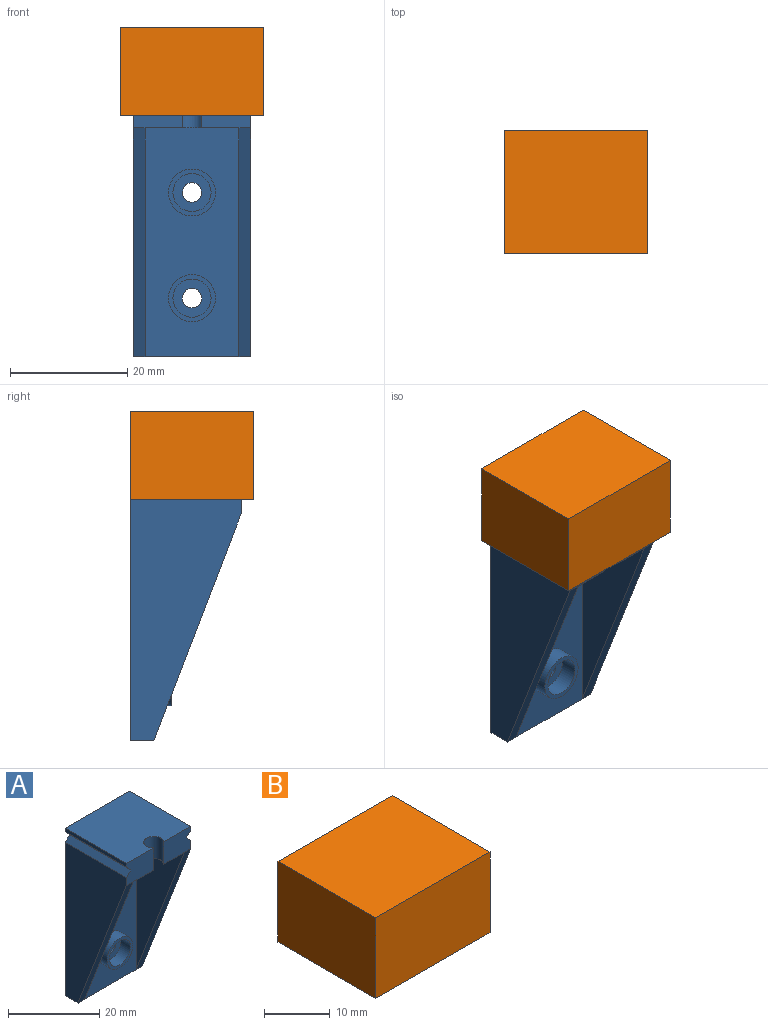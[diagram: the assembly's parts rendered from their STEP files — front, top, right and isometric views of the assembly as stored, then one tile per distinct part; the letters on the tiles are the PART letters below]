
ASSEMBLY  parts=2 mates=1
PART A: 30 faces, bbox 20x19x45 mm
  f0: plane 8.39x6mm, normal (0,-1,0), area 48.3mm2, adj f2,f4,f5,f11,f12,f13,f27,f29
  f1: plane 8.39x6mm, normal (0,-1,0), area 48.3mm2, adj f2,f5,f6,f7,f8,f9,f28,f29
  f2: plane 16x15mm, normal (0,0,-1), area 226.4mm2, adj f0,f1,f3,f25,f26,f29
  f3: plane 39x16mm, normal (0,-1,0), area 523.5mm2, adj f2,f10,f15,f17,f25,f26
  f4: plane 19x1mm, normal (1,0,0), area 19mm2, adj f0,f5,f13,f14
  f5: plane 20x19mm, normal (0,0,1), area 366.4mm2, adj f0,f1,f4,f6,f14,f29
  f6: plane 19x1mm, normal (-1,0,0), area 19mm2, adj f1,f5,f7,f14
  f7: plane 19x1.41mm, normal (-0.71,0,-0.71), area 38mm2, adj f1,f6,f8,f14
  f8: plane 19x1.41mm, normal (-0.71,0,0.71), area 38mm2, adj f1,f7,f9,f14
  f9: plane 41.17x19mm, normal (-1,0,0), area 489.8mm2, adj f1,f8,f10,f14,f28
  f10: plane 20x4mm, normal (0,0,-1), area 80mm2, adj f3,f9,f11,f14,f27,f28
  f11: plane 41.17x19mm, normal (1,0,0), area 489.8mm2, adj f0,f10,f12,f14,f27
  f12: plane 19x1.41mm, normal (0.71,0,0.71), area 38mm2, adj f0,f11,f13,f14
  f13: plane 19x1.41mm, normal (0.71,0,-0.71), area 38mm2, adj f0,f4,f12,f14
  f14: plane 45x20mm, normal (0,1,0), area 878.9mm2, adj f4,f5,f6,f7,f8,f9,f10,f11
  f15: cylinder r=4mm len=8mm, axis (0,1,0), area 75.4mm2, adj f3,f16
  f16: plane 8x8mm, normal (0,-1,0), area 17.1mm2, adj f15,f21
  f17: cylinder r=4mm len=8mm, axis (0,1,0), area 75.4mm2, adj f3,f18
  f18: plane 8x8mm, normal (0,-1,0), area 17.1mm2, adj f17,f24
  f19: cylinder r=1.65mm len=4mm, axis (0,-1,0), area 41.5mm2, adj f14,f20
  f20: plane 6.5x6.5mm, normal (0,-1,0), area 24.6mm2, adj f19,f21
  f21: cylinder r=3.25mm len=6.5mm, axis (0,-1,0), area 61.3mm2, adj f16,f20
  f22: cylinder r=1.65mm len=4mm, axis (0,-1,0), area 41.5mm2, adj f14,f23
  f23: plane 6.5x6.5mm, normal (0,-1,0), area 24.6mm2, adj f22,f24
  f24: cylinder r=3.25mm len=6.5mm, axis (0,-1,0), area 61.3mm2, adj f18,f23
  f25: plane 39x15mm, normal (1,0,0), area 292.5mm2, adj f2,f3,f28
  f26: plane 39x15mm, normal (-1,0,0), area 292.5mm2, adj f2,f3,f27
  f27: plane 39x15mm, normal (0,-0.93,-0.36), area 83.6mm2, adj f0,f10,f11,f26
  f28: plane 39x15mm, normal (0,-0.93,-0.36), area 83.6mm2, adj f1,f9,f10,f25
  f29: cylinder r=2.2mm len=6mm, axis (0,0,1), area 61.3mm2, adj f0,f1,f2,f5
PART B: 14 faces, bbox 24.5x21x15 mm
  f0: plane 20.5x13mm, normal (0,1,0), area 262.5mm2, adj f6,f7,f8,f9,f10,f11,f12,f13
  f1: plane 24.5x15mm, normal (0,-1,0), area 367.5mm2, adj f2,f4,f5,f6
  f2: plane 21x15mm, normal (1,0,0), area 315mm2, adj f1,f3,f5,f6
  f3: plane 24.5x15mm, normal (0,1,0), area 105mm2, adj f2,f4,f5,f6,f7,f8,f9,f10
  f4: plane 21x15mm, normal (-1,0,0), area 315mm2, adj f1,f3,f5,f6
  f5: plane 24.5x21mm, normal (0,0,1), area 514.5mm2, adj f1,f2,f3,f4
  f6: plane 24.5x21mm, normal (0,0,-1), area 125mm2, adj f0,f1,f2,f3,f4,f10,f12
  f7: plane 19x10.17mm, normal (-1,0,0), area 193.3mm2, adj f0,f3,f9,f11
  f8: plane 19x10.17mm, normal (1,0,0), area 193.3mm2, adj f0,f3,f9,f13
  f9: plane 20.5x19mm, normal (0,0,-1), area 389.5mm2, adj f0,f3,f7,f8
  f10: plane 19x1.41mm, normal (-0.71,0,-0.71), area 38mm2, adj f0,f3,f6,f11
  f11: plane 19x1.41mm, normal (-0.71,0,0.71), area 38mm2, adj f0,f3,f7,f10
  f12: plane 19x1.41mm, normal (0.71,0,-0.71), area 38mm2, adj f0,f3,f6,f13
  f13: plane 19x1.41mm, normal (0.71,0,0.71), area 38mm2, adj f0,f3,f8,f12
PLACE A t=(-28.46,-8.81,-2.81)mm
PLACE B t=(-28.46,-19.31,15.86)mm
MATE slider B.f3 <-> A.f14  axis (0,-1,0) through (-19.63,-8.81,17.28)mm
